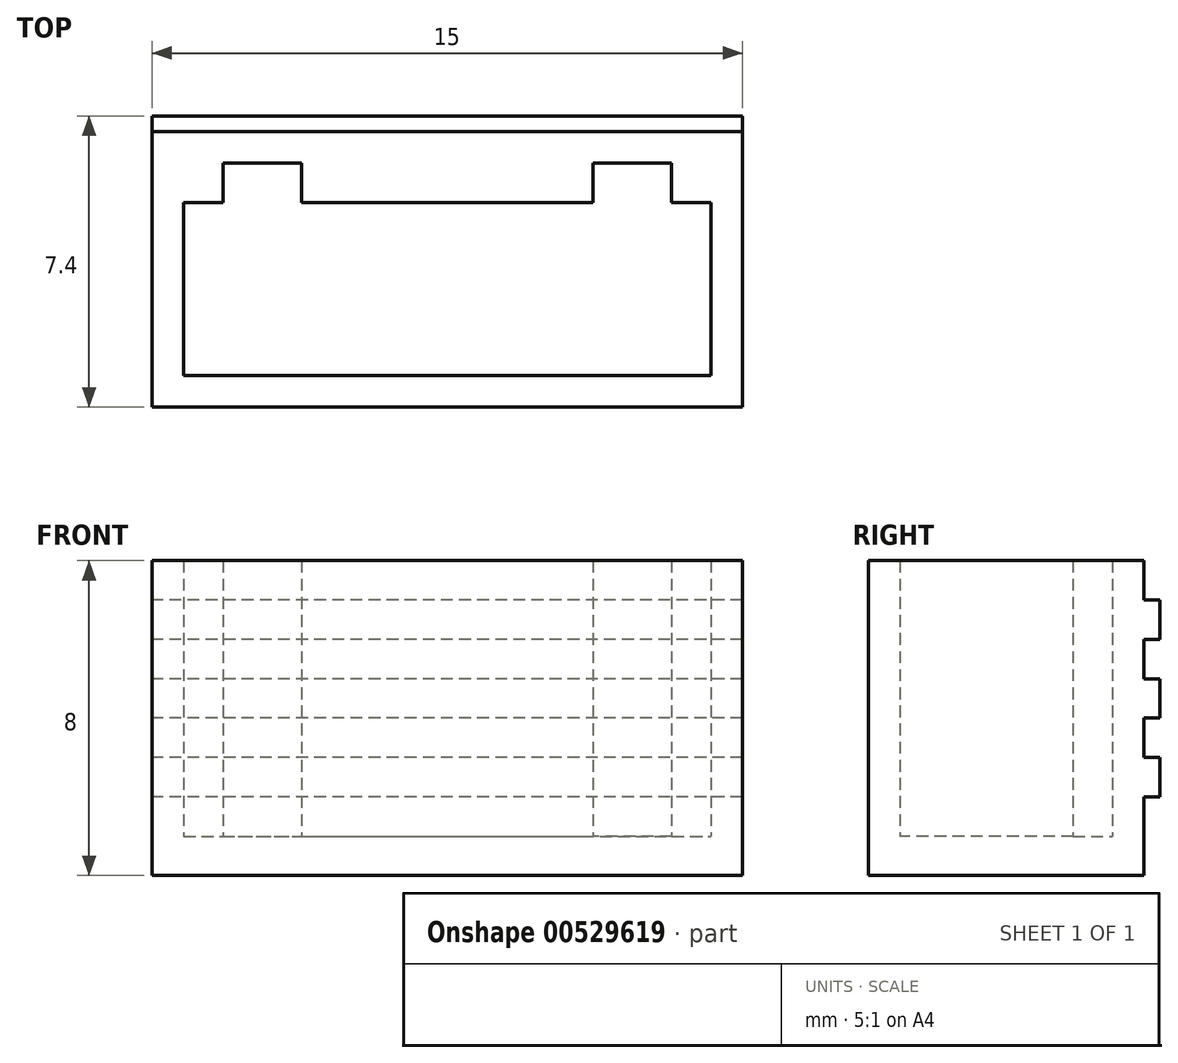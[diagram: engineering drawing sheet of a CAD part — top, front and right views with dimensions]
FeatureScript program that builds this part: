
annotation { "Feature Type Name" : "Feature", "Feature Type Description" : "" }
export const myFeature = defineFeature(function(context is Context, id is Id, definition is map)
    precondition{}
    {
        {
            var Q0;
            Q0=qCreatedBy(makeId("Top.planeOp"),FACE);
            var sketch = newSketch(context, id + "F0", { "sketchPlane" : qUnion([Q0])});
            skLineSegment(sketch, "E0.bottom", {"start": v(7.5, 3.5) * mm, "end": v(-7.5, 3.5) * mm});
            skLineSegment(sketch, "E0.top", {"start": v(7.5, -3.5) * mm, "end": v(-7.5, -3.5) * mm});
            skLineSegment(sketch, "E0.left", {"start": v(7.5, 3.5) * mm, "end": v(7.5, -3.5) * mm});
            skLineSegment(sketch, "E0.right", {"start": v(-7.5, 3.5) * mm, "end": v(-7.5, -3.5) * mm});
            skPoint(sketch, "E0.middle", {"position": v(0, 0) * mm});
            skSolve(sketch);
        }
        {
            var Q0;
            Q0=makeQuery(id+"F0.imprint","IMPRINT",FACE,{"disambiguationData":[TD([[makeQuery(id+"F0.imprint","IMPRINT",EDGE,{"derivedFrom":sQuery(id+"F0.wireOp",EDGE,"E0.bottom")}),1.0]])]});
            extrude(context, id + "F1", {"entities" : qUnion([Q0]), "depth" : 1 * mm, "offsetDistance" : 25 * mm});
        }
        {
            var Q0;
            Q0=makeQuery(id+"F1.opExtrude","CAP_FACE",FACE,{"disambiguationData":[OSD([sQuery(id+"F0.wireOp",EDGE,"E0.bottom"),sQuery(id+"F0.wireOp",EDGE,"E0.top"),sQuery(id+"F0.wireOp",EDGE,"E0.left"),sQuery(id+"F0.wireOp",EDGE,"E0.right")])],"isStart":false});
            var sketch = newSketch(context, id + "F2", { "sketchPlane" : qUnion([Q0])});
            skLineSegment(sketch, "E1.bottom", {"start": v(-6.7, 1.7) * mm, "end": v(6.7, 1.7) * mm});
            skLineSegment(sketch, "E1.top", {"start": v(-6.7, -2.7) * mm, "end": v(6.7, -2.7) * mm});
            skLineSegment(sketch, "E1.left", {"start": v(-6.7, 1.7) * mm, "end": v(-6.7, -2.7) * mm});
            skLineSegment(sketch, "E1.right", {"start": v(6.7, 1.7) * mm, "end": v(6.7, -2.7) * mm});
            skLineSegment(sketch, "E2.bottom", {"start": v(-5.7, 1.7) * mm, "end": v(-3.7, 1.7) * mm});
            skLineSegment(sketch, "E2.top", {"start": v(-5.7, 2.7) * mm, "end": v(-3.7, 2.7) * mm});
            skLineSegment(sketch, "E2.left", {"start": v(-5.7, 1.7) * mm, "end": v(-5.7, 2.7) * mm});
            skLineSegment(sketch, "E2.right", {"start": v(-3.7, 1.7) * mm, "end": v(-3.7, 2.7) * mm});
            skLineSegment(sketch, "E3", {"start": v(0, -3.5) * mm, "end": v(0, 3.5) * mm, "construction": true});
            skLineSegment(sketch, "E4.MirrorCS", {"start": v(5.7, 2.7) * mm, "end": v(3.7, 2.7) * mm});
            skLineSegment(sketch, "E5.MirrorCS", {"start": v(5.7, 1.7) * mm, "end": v(5.7, 2.7) * mm});
            skLineSegment(sketch, "E6.MirrorCS", {"start": v(3.7, 1.7) * mm, "end": v(3.7, 2.7) * mm});
            skLineSegment(sketch, "E7.MirrorCS", {"start": v(5.7, 1.7) * mm, "end": v(3.7, 1.7) * mm});
            skSolve(sketch);
        }
        {
            var Q0;
            Q0=makeQuery(id+"F2.imprint","IMPRINT",FACE,{"disambiguationData":[TD([[makeQuery(id+"F2.imprint","IMPRINT",EDGE,{"derivedFrom":sQuery(id+"F2.wireOp",EDGE,"E1.top")}),-1.0]])]});
            extrude(context, id + "F3", {"entities" : qUnion([Q0]), "operationType" : NewBodyOperationType.ADD, "depth" : 7 * mm, "offsetDistance" : 25 * mm});
        }
        {
            var Q0;
            {var subQ0=sQuery(id+"F0.wireOp",EDGE,"E0.bottom");Q0=makeQuery(id+"F3.boolean.opBoolean","MERGE",FACE,{"derivedFrom":[makeQuery(id+"F1.opExtrude","SWEPT_FACE",FACE,{"disambiguationData":[OSD([subQ0])]}),makeQuery(id+"F3.opExtrude","SWEPT_FACE",FACE,{"disambiguationData":[OSD([subQ0])]})]});}
            var sketch = newSketch(context, id + "F4", { "sketchPlane" : qUnion([Q0])});
            skLineSegment(sketch, "E8.bottom", {"start": v(-7.5, 7) * mm, "end": v(7.5, 7) * mm});
            skLineSegment(sketch, "E8.top", {"start": v(-7.5, 6) * mm, "end": v(7.5, 6) * mm});
            skLineSegment(sketch, "E8.left", {"start": v(-7.5, 7) * mm, "end": v(-7.5, 6) * mm});
            skLineSegment(sketch, "E8.right", {"start": v(7.5, 7) * mm, "end": v(7.5, 6) * mm});
            skLineSegment(sketch, "E9.1.0.0", {"start": v(7.5, 5) * mm, "end": v(7.5, 4) * mm});
            skLineSegment(sketch, "E9.1.0.1", {"start": v(-7.5, 4) * mm, "end": v(7.5, 4) * mm});
            skLineSegment(sketch, "E9.1.0.2", {"start": v(-7.5, 5) * mm, "end": v(7.5, 5) * mm});
            skLineSegment(sketch, "E9.1.0.3", {"start": v(-7.5, 5) * mm, "end": v(-7.5, 4) * mm});
            skLineSegment(sketch, "E9.2.0.0", {"start": v(7.5, 3) * mm, "end": v(7.5, 2) * mm});
            skLineSegment(sketch, "E9.2.0.1", {"start": v(-7.5, 2) * mm, "end": v(7.5, 2) * mm});
            skLineSegment(sketch, "E9.2.0.2", {"start": v(-7.5, 3) * mm, "end": v(7.5, 3) * mm});
            skLineSegment(sketch, "E9.2.0.3", {"start": v(-7.5, 3) * mm, "end": v(-7.5, 2) * mm});
            skLineSegment(sketch, "E9.direction1", {"start": v(7.5, 6) * mm, "end": v(7.5, 4) * mm, "construction": true});
            skSolve(sketch);
        }
        {
            var Q0;
            Q0 = qSketchRegion(id + "F4", true);
            var Q1;
            Q1=makeQuery(id+"F4.imprint","IMPRINT",FACE,{"disambiguationData":[TD([[makeQuery(id+"F4.imprint","IMPRINT",EDGE,{"derivedFrom":sQuery(id+"F4.wireOp",EDGE,"E8.bottom")}),-1.0]])]});
            extrude(context, id + "F5", {"entities" : qUnion([Q0, Q1]), "operationType" : NewBodyOperationType.ADD, "depth" : .4 * mm, "offsetDistance" : 25 * mm});
        }
    });
